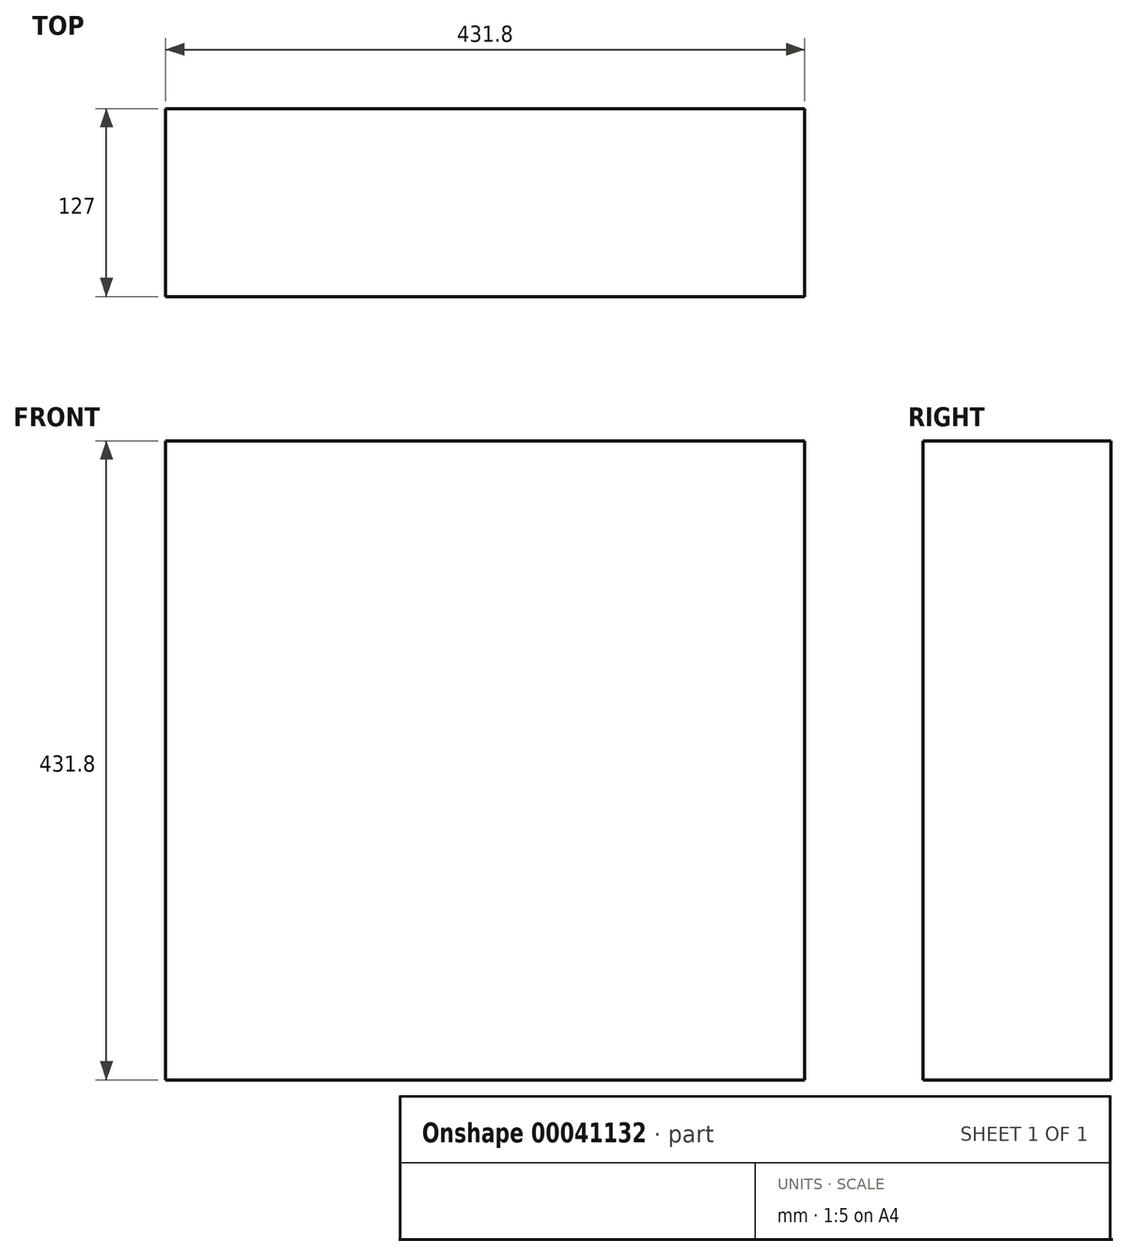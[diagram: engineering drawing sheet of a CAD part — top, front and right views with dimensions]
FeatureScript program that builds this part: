
annotation { "Feature Type Name" : "Feature", "Feature Type Description" : "" }
export const myFeature = defineFeature(function(context is Context, id is Id, definition is map)
    precondition{}
    {
        {
            var Q0;
            Q0=qCreatedBy(makeId("Front.planeOp"),FACE);
            var sketch = newSketch(context, id + "F0", { "sketchPlane" : qUnion([Q0])});
            skLineSegment(sketch, "E0.bottom", {"start": v(-41.87, 392.78) * mm, "end": v(389.93, 392.78) * mm});
            skLineSegment(sketch, "E0.top", {"start": v(-41.87, -39.02) * mm, "end": v(389.93, -39.02) * mm});
            skLineSegment(sketch, "E0.left", {"start": v(-41.87, 392.78) * mm, "end": v(-41.87, -39.02) * mm});
            skLineSegment(sketch, "E0.right", {"start": v(389.93, 392.78) * mm, "end": v(389.93, -39.02) * mm});
            skSolve(sketch);
        }
        {
            var Q0;
            Q0 = qSketchRegion(id + "F0", true);
            extrude(context, id + "F1", {"entities" : qUnion([Q0]), "depth" : 127 * mm});
        }
    });
